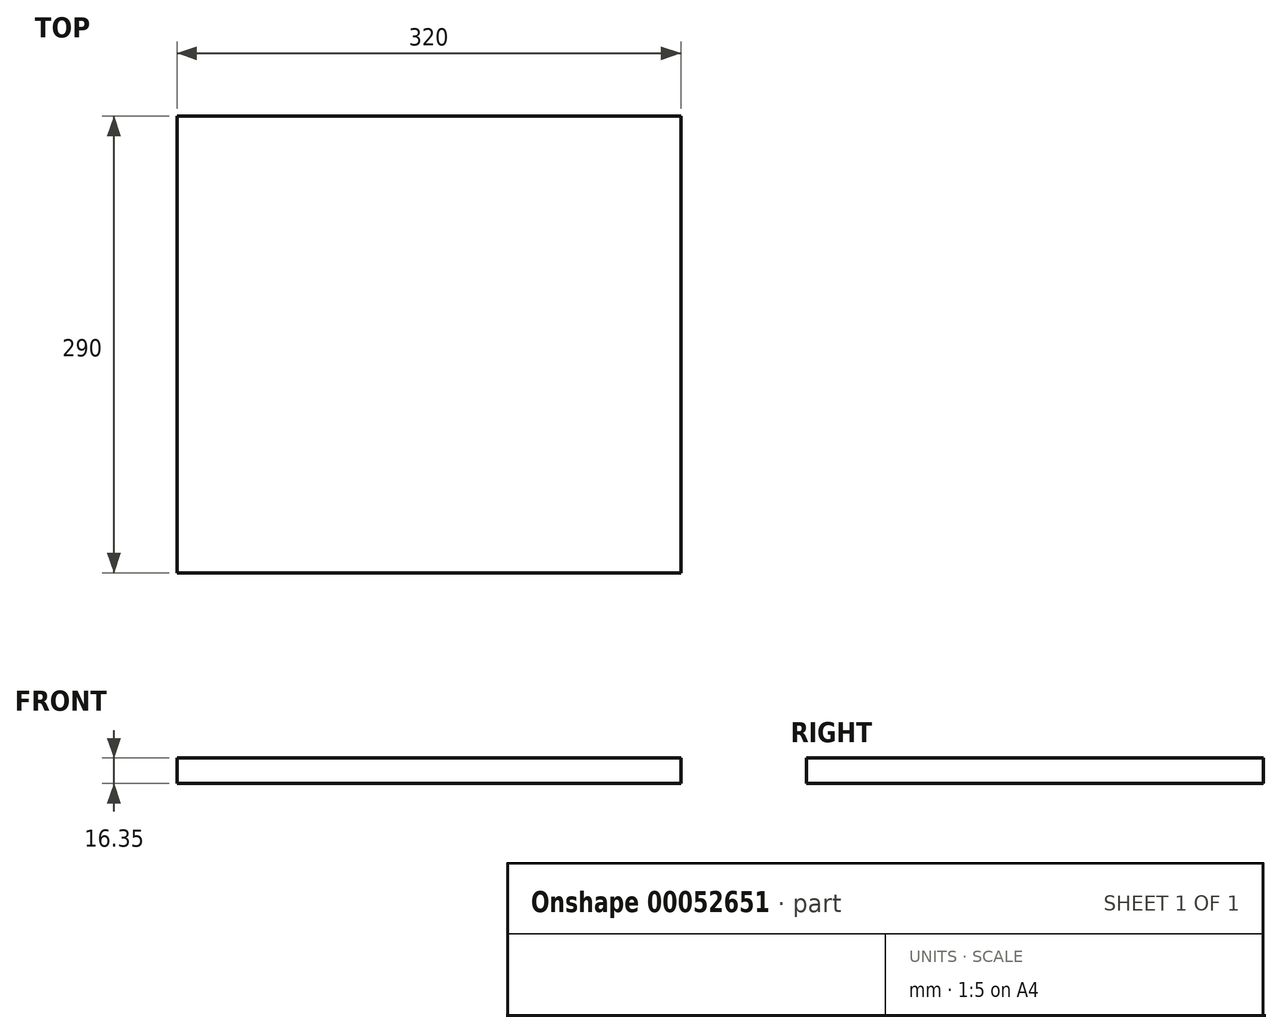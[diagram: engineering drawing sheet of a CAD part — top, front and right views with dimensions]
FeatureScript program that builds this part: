
annotation { "Feature Type Name" : "Feature", "Feature Type Description" : "" }
export const myFeature = defineFeature(function(context is Context, id is Id, definition is map)
    precondition{}
    {
        {
            var Q0;
            Q0=qCreatedBy(makeId("Top.planeOp"),FACE);
            var sketch = newSketch(context, id + "F0", { "sketchPlane" : qUnion([Q0])});
            skLineSegment(sketch, "E0.bottom", {"start": v(-70.96, 65.05) * mm, "end": v(249.04, 65.05) * mm});
            skLineSegment(sketch, "E0.top", {"start": v(-70.96, -224.95) * mm, "end": v(249.04, -224.95) * mm});
            skLineSegment(sketch, "E0.left", {"start": v(-70.96, 65.05) * mm, "end": v(-70.96, -224.95) * mm});
            skLineSegment(sketch, "E0.right", {"start": v(249.04, 65.05) * mm, "end": v(249.04, -224.95) * mm});
            skSolve(sketch);
        }
        {
            var Q0;
            Q0=qSketchRegion(id+"F0",true);
            extrude(context, id + "F1", {"entities" : qUnion([Q0]), "depth" : 16.35 * mm});
        }
    });
